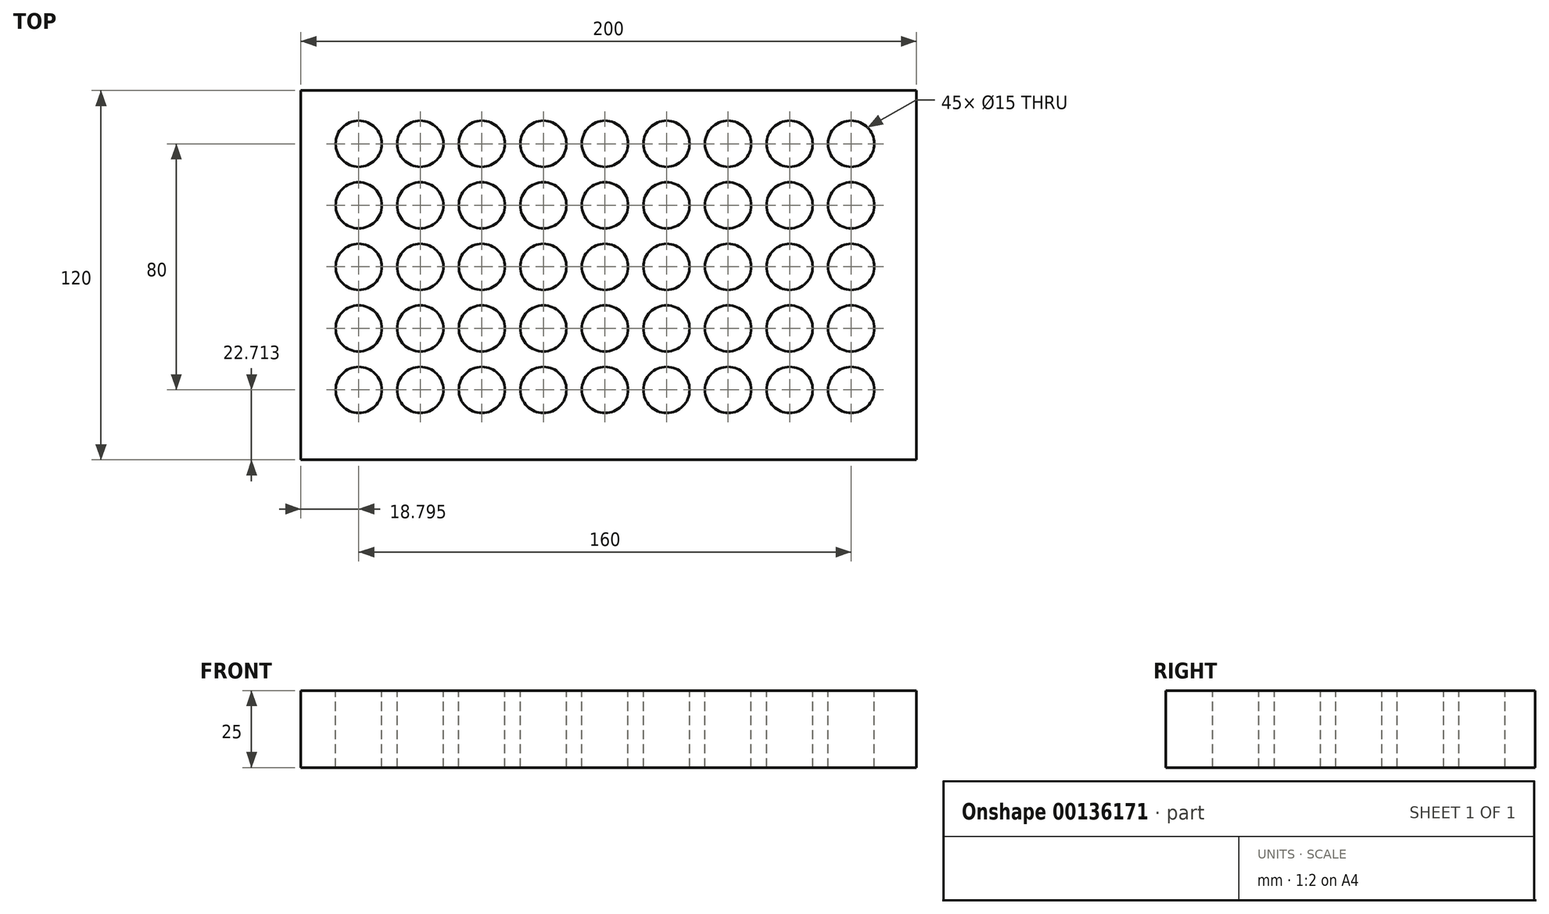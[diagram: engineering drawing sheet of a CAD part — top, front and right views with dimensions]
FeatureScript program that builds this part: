
annotation { "Feature Type Name" : "Feature", "Feature Type Description" : "" }
export const myFeature = defineFeature(function(context is Context, id is Id, definition is map)
    precondition{}
    {
        {
            var Q0;
            Q0=qCreatedBy(makeId("Top.planeOp"),FACE);
            var sketch = newSketch(context, id + "F0", { "sketchPlane" : qUnion([Q0])});
            skLineSegment(sketch, "E0.bottom", {"start": v(-100, 60) * mm, "end": v(100, 60) * mm});
            skLineSegment(sketch, "E0.top", {"start": v(-100, -60) * mm, "end": v(100, -60) * mm});
            skLineSegment(sketch, "E0.left", {"start": v(-100, 60) * mm, "end": v(-100, -60) * mm});
            skLineSegment(sketch, "E0.right", {"start": v(100, 60) * mm, "end": v(100, -60) * mm});
            skPoint(sketch, "E0.middle", {"position": v(0, 0) * mm});
            skSolve(sketch);
        }
        {
            var Q0;
            Q0=makeQuery(id+"F0.imprint","IMPRINT",FACE,{"disambiguationData":[TD([[makeQuery(id+"F0.imprint","IMPRINT",EDGE,{"derivedFrom":sQuery(id+"F0.wireOp",EDGE,"E0.bottom")}),-1.0]])]});
            extrude(context, id + "F1", {"entities" : qUnion([Q0]), "depth" : 25 * mm});
        }
        {
            var Q0;
            Q0=makeQuery(id+"F1.opExtrude","CAP_FACE",FACE,{"disambiguationData":[OSD([sQuery(id+"F0.wireOp",EDGE,"E0.bottom"),sQuery(id+"F0.wireOp",EDGE,"E0.top"),sQuery(id+"F0.wireOp",EDGE,"E0.left"),sQuery(id+"F0.wireOp",EDGE,"E0.right")])],"isStart":false});
            var sketch = newSketch(context, id + "F2", { "sketchPlane" : qUnion([Q0])});
            skCircle(sketch, "E1", {"center": v(-81.2, 42.71) * mm, "radius": 7.5 * mm});
            skCircle(sketch, "E2.0.1.0", {"center": v(-81.2, 22.71) * mm, "radius": 7.5 * mm});
            skCircle(sketch, "E2.0.2.0", {"center": v(-81.2, 2.71) * mm, "radius": 7.5 * mm});
            skCircle(sketch, "E2.0.3.0", {"center": v(-81.2, -17.29) * mm, "radius": 7.5 * mm});
            skCircle(sketch, "E2.0.4.0", {"center": v(-81.2, -37.29) * mm, "radius": 7.5 * mm});
            skCircle(sketch, "E2.1.0.0", {"center": v(-61.2, 42.71) * mm, "radius": 7.5 * mm});
            skCircle(sketch, "E2.1.1.0", {"center": v(-61.2, 22.71) * mm, "radius": 7.5 * mm});
            skCircle(sketch, "E2.1.2.0", {"center": v(-61.2, 2.71) * mm, "radius": 7.5 * mm});
            skCircle(sketch, "E2.1.3.0", {"center": v(-61.2, -17.29) * mm, "radius": 7.5 * mm});
            skCircle(sketch, "E2.1.4.0", {"center": v(-61.2, -37.29) * mm, "radius": 7.5 * mm});
            skCircle(sketch, "E2.2.0.0", {"center": v(-41.2, 42.71) * mm, "radius": 7.5 * mm});
            skCircle(sketch, "E2.2.1.0", {"center": v(-41.2, 22.71) * mm, "radius": 7.5 * mm});
            skCircle(sketch, "E2.2.2.0", {"center": v(-41.2, 2.71) * mm, "radius": 7.5 * mm});
            skCircle(sketch, "E2.2.3.0", {"center": v(-41.2, -17.29) * mm, "radius": 7.5 * mm});
            skCircle(sketch, "E2.2.4.0", {"center": v(-41.2, -37.29) * mm, "radius": 7.5 * mm});
            skCircle(sketch, "E2.3.0.0", {"center": v(-21.2, 42.71) * mm, "radius": 7.5 * mm});
            skCircle(sketch, "E2.3.1.0", {"center": v(-21.2, 22.71) * mm, "radius": 7.5 * mm});
            skCircle(sketch, "E2.3.2.0", {"center": v(-21.2, 2.71) * mm, "radius": 7.5 * mm});
            skCircle(sketch, "E2.3.3.0", {"center": v(-21.2, -17.29) * mm, "radius": 7.5 * mm});
            skCircle(sketch, "E2.3.4.0", {"center": v(-21.2, -37.29) * mm, "radius": 7.5 * mm});
            skCircle(sketch, "E2.4.0.0", {"center": v(-1.2, 42.71) * mm, "radius": 7.5 * mm});
            skCircle(sketch, "E2.4.1.0", {"center": v(-1.2, 22.71) * mm, "radius": 7.5 * mm});
            skCircle(sketch, "E2.4.2.0", {"center": v(-1.2, 2.71) * mm, "radius": 7.5 * mm});
            skCircle(sketch, "E2.4.3.0", {"center": v(-1.2, -17.29) * mm, "radius": 7.5 * mm});
            skCircle(sketch, "E2.4.4.0", {"center": v(-1.2, -37.29) * mm, "radius": 7.5 * mm});
            skCircle(sketch, "E2.5.0.0", {"center": v(18.8, 42.71) * mm, "radius": 7.5 * mm});
            skCircle(sketch, "E2.5.1.0", {"center": v(18.8, 22.71) * mm, "radius": 7.5 * mm});
            skCircle(sketch, "E2.5.2.0", {"center": v(18.8, 2.71) * mm, "radius": 7.5 * mm});
            skCircle(sketch, "E2.5.3.0", {"center": v(18.8, -17.29) * mm, "radius": 7.5 * mm});
            skCircle(sketch, "E2.5.4.0", {"center": v(18.8, -37.29) * mm, "radius": 7.5 * mm});
            skCircle(sketch, "E2.6.0.0", {"center": v(38.8, 42.71) * mm, "radius": 7.5 * mm});
            skCircle(sketch, "E2.6.1.0", {"center": v(38.8, 22.71) * mm, "radius": 7.5 * mm});
            skCircle(sketch, "E2.6.2.0", {"center": v(38.8, 2.71) * mm, "radius": 7.5 * mm});
            skCircle(sketch, "E2.6.3.0", {"center": v(38.8, -17.29) * mm, "radius": 7.5 * mm});
            skCircle(sketch, "E2.6.4.0", {"center": v(38.8, -37.29) * mm, "radius": 7.5 * mm});
            skCircle(sketch, "E2.7.0.0", {"center": v(58.8, 42.71) * mm, "radius": 7.5 * mm});
            skCircle(sketch, "E2.7.1.0", {"center": v(58.8, 22.71) * mm, "radius": 7.5 * mm});
            skCircle(sketch, "E2.7.2.0", {"center": v(58.8, 2.71) * mm, "radius": 7.5 * mm});
            skCircle(sketch, "E2.7.3.0", {"center": v(58.8, -17.29) * mm, "radius": 7.5 * mm});
            skCircle(sketch, "E2.7.4.0", {"center": v(58.8, -37.29) * mm, "radius": 7.5 * mm});
            skCircle(sketch, "E2.8.0.0", {"center": v(78.8, 42.71) * mm, "radius": 7.5 * mm});
            skCircle(sketch, "E2.8.1.0", {"center": v(78.8, 22.71) * mm, "radius": 7.5 * mm});
            skCircle(sketch, "E2.8.2.0", {"center": v(78.8, 2.71) * mm, "radius": 7.5 * mm});
            skCircle(sketch, "E2.8.3.0", {"center": v(78.8, -17.29) * mm, "radius": 7.5 * mm});
            skCircle(sketch, "E2.8.4.0", {"center": v(78.8, -37.29) * mm, "radius": 7.5 * mm});
            skLineSegment(sketch, "E2.direction1", {"start": v(-81.2, 42.71) * mm, "end": v(-61.2, 42.71) * mm, "construction": true});
            skLineSegment(sketch, "E2.direction2", {"start": v(-81.2, 42.71) * mm, "end": v(-81.2, 22.71) * mm, "construction": true});
            skSolve(sketch);
        }
        {
            var Q0;
            Q0 = qSketchRegion(id + "F2", true);
            extrude(context, id + "F3", {"entities" : qUnion([Q0]), "operationType" : NewBodyOperationType.REMOVE, "oppositeDirection" : true, "depth" : 25 * mm});
        }
    });
